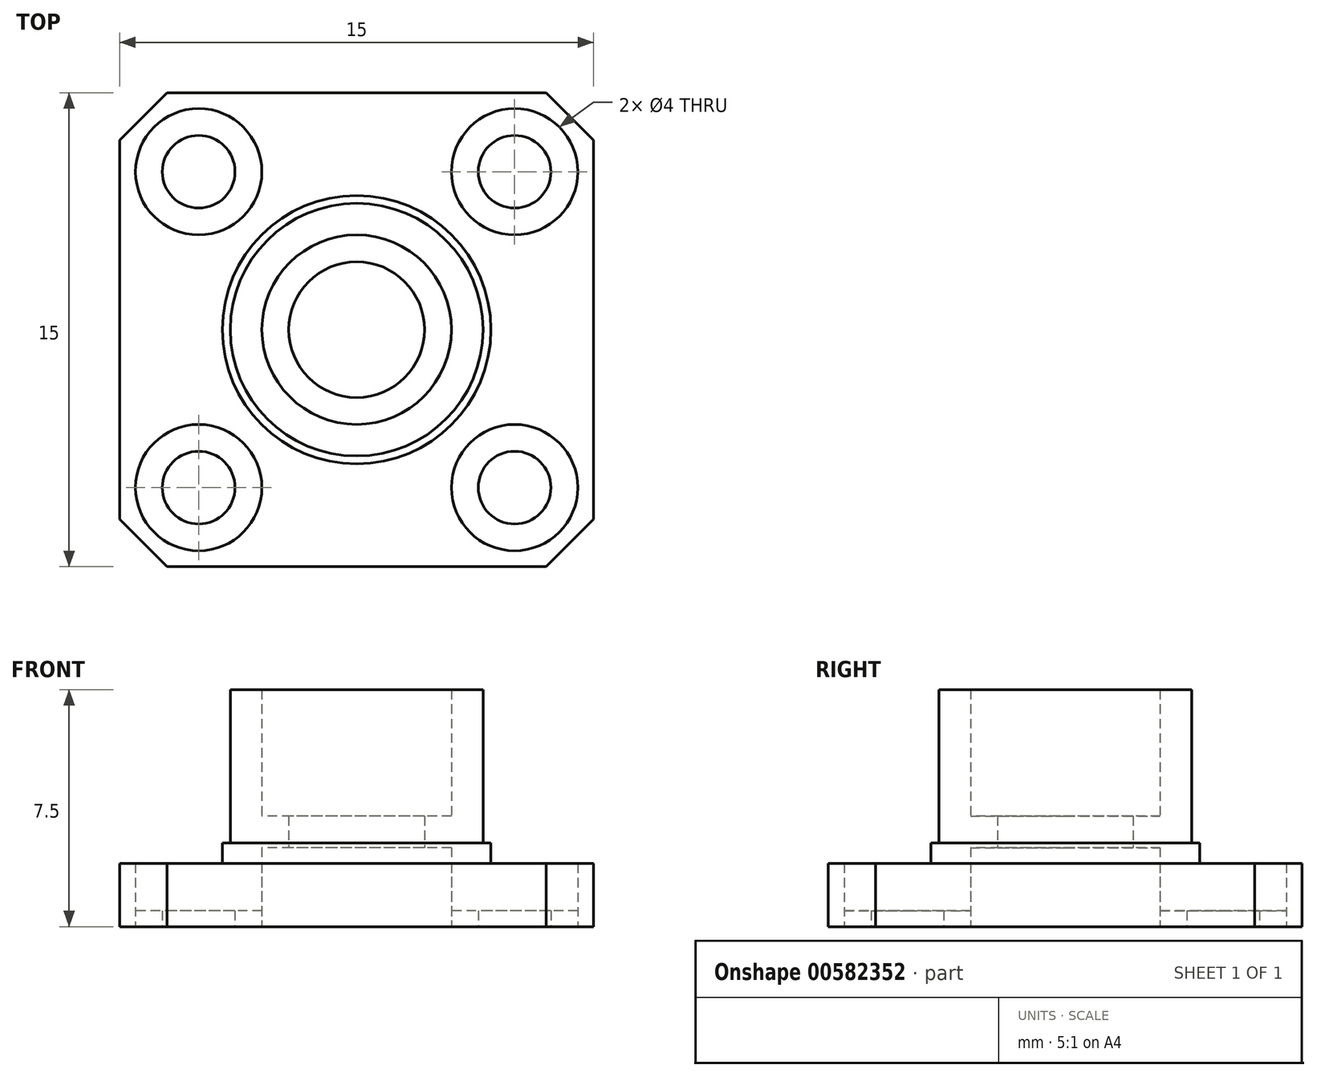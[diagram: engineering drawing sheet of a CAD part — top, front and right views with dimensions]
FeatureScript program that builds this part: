
annotation { "Feature Type Name" : "Feature", "Feature Type Description" : "" }
export const myFeature = defineFeature(function(context is Context, id is Id, definition is map)
    precondition{}
    {
        {
            var Q0;
            Q0=qCreatedBy(makeId("Top.planeOp"),FACE);
            var sketch = newSketch(context, id + "F0", { "sketchPlane" : qUnion([Q0])});
            skLineSegment(sketch, "E0.bottom", {"start": v(7.5, -7.5) * mm, "end": v(-7.5, -7.5) * mm});
            skLineSegment(sketch, "E0.top", {"start": v(7.5, 7.5) * mm, "end": v(-7.5, 7.5) * mm});
            skLineSegment(sketch, "E0.left", {"start": v(7.5, -7.5) * mm, "end": v(7.5, 7.5) * mm});
            skLineSegment(sketch, "E0.right", {"start": v(-7.5, -7.5) * mm, "end": v(-7.5, 7.5) * mm});
            skPoint(sketch, "E0.middle", {"position": v(0, 0) * mm});
            skCircle(sketch, "E1", {"center": v(0, 0) * mm, "radius": 4.25 * mm});
            skCircle(sketch, "E2", {"center": v(0, 0) * mm, "radius": 4 * mm});
            skCircle(sketch, "E3", {"center": v(0, 0) * mm, "radius": 3 * mm});
            skCircle(sketch, "E4", {"center": v(0, 0) * mm, "radius": 2.15 * mm});
            skCircle(sketch, "E5", {"center": v(-5, 5) * mm, "radius": 1.15 * mm});
            skCircle(sketch, "E6.MirrorC", {"center": v(5, 5) * mm, "radius": 1.15 * mm});
            skCircle(sketch, "E7.MirrorC", {"center": v(5, -5) * mm, "radius": 1.15 * mm});
            skCircle(sketch, "E8.MirrorC", {"center": v(-5, -5) * mm, "radius": 1.15 * mm});
            skCircle(sketch, "E9.0", {"center": v(0, 0) * mm, "radius": 3.76 * mm});
            skCircle(sketch, "E10", {"center": v(-5, 5) * mm, "radius": 2 * mm});
            skCircle(sketch, "E11", {"center": v(5, 5) * mm, "radius": 2 * mm});
            skCircle(sketch, "E12", {"center": v(-5, -5) * mm, "radius": 2 * mm});
            skCircle(sketch, "E13", {"center": v(5, -5) * mm, "radius": 2 * mm});
            skSolve(sketch);
        }
        {
            var Q0;
            Q0=makeQuery(id+"F0.imprint","IMPRINT",FACE,{"disambiguationData":[TD([[makeQuery(id+"F0.imprint","IMPRINT",EDGE,{"derivedFrom":sQuery(id+"F0.wireOp",EDGE,"E0.bottom")}),-1.0]])]});
            extrude(context, id + "F1", {"entities" : qUnion([Q0]), "depth" : 2 * mm, "offsetDistance" : 25 * mm});
        }
        {
            var Q0;
            Q0=makeQuery(id+"F0.imprint","IMPRINT",FACE,{"disambiguationData":[TD([[makeQuery(id+"F0.imprint","IMPRINT",EDGE,{"derivedFrom":sQuery(id+"F0.wireOp",EDGE,"E1")}),1.0]])]});
            extrude(context, id + "F2", {"entities" : qUnion([Q0]), "operationType" : NewBodyOperationType.ADD, "depth" : 2.65 * mm, "offsetDistance" : 25 * mm});
        }
        {
            var Q0;
            Q0=makeQuery(id+"F0.imprint","IMPRINT",FACE,{"disambiguationData":[TD([[makeQuery(id+"F0.imprint","IMPRINT",EDGE,{"derivedFrom":sQuery(id+"F0.wireOp",EDGE,"E2")}),1.0]])]});
            var Q1;
            Q1=makeQuery(id+"F0.imprint","IMPRINT",FACE,{"disambiguationData":[TD([[makeQuery(id+"F0.imprint","IMPRINT",EDGE,{"derivedFrom":sQuery(id+"F0.wireOp",EDGE,"E3")}),-1.0]])]});
            extrude(context, id + "F3", {"entities" : qUnion([Q0, Q1]), "operationType" : NewBodyOperationType.ADD, "depth" : 7.5 * mm, "offsetDistance" : 25 * mm});
        }
        {
            var Q0;
            Q0=makeQuery(id+"F0.imprint","IMPRINT",FACE,{"disambiguationData":[TD([[makeQuery(id+"F0.imprint","IMPRINT",EDGE,{"derivedFrom":sQuery(id+"F0.wireOp",EDGE,"E3")}),1.0]])]});
            var Q1;
            Q1=makeQuery(id+"F0.imprint","IMPRINT",FACE,{"disambiguationData":[TD([[makeQuery(id+"F0.imprint","IMPRINT",EDGE,{"derivedFrom":sQuery(id+"F0.wireOp",EDGE,"E3")}),-1.0]])]});
            extrude(context, id + "F4", {"entities" : qUnion([Q0, Q1]), "operationType" : NewBodyOperationType.ADD, "depth" : (7.5 - 4) * mm, "offsetDistance" : 25 * mm});
        }
        {
            var Q0;
            Q0=makeQuery(id+"F0.imprint","IMPRINT",FACE,{"disambiguationData":[TD([[makeQuery(id+"F0.imprint","IMPRINT",EDGE,{"derivedFrom":sQuery(id+"F0.wireOp",EDGE,"E3")}),1.0]])]});
            extrude(context, id + "F5", {"entities" : qUnion([Q0]), "operationType" : NewBodyOperationType.REMOVE, "depth" : 2.5 * mm, "offsetDistance" : 25 * mm});
        }
        {
            var Q0;
            Q0=makeQuery(id+"F1.opExtrude","SWEPT_EDGE",EDGE,{"disambiguationData":[OSD([sQuery(id+"F0.wireOp",EDGE,"E0.bottom"),sQuery(id+"F0.wireOp",EDGE,"E0.left")])]});
            var Q1;
            Q1=makeQuery(id+"F1.opExtrude","SWEPT_EDGE",EDGE,{"disambiguationData":[OSD([sQuery(id+"F0.wireOp",EDGE,"E0.top"),sQuery(id+"F0.wireOp",EDGE,"E0.left")])]});
            var Q2;
            Q2=makeQuery(id+"F1.opExtrude","SWEPT_EDGE",EDGE,{"disambiguationData":[OSD([sQuery(id+"F0.wireOp",EDGE,"E0.bottom"),sQuery(id+"F0.wireOp",EDGE,"E0.right")])]});
            var Q3;
            Q3=makeQuery(id+"F1.opExtrude","SWEPT_EDGE",EDGE,{"disambiguationData":[OSD([sQuery(id+"F0.wireOp",EDGE,"E0.top"),sQuery(id+"F0.wireOp",EDGE,"E0.right")])]});
            chamfer(context, id + "F6", {"entities" : qUnion([Q0, Q1, Q2, Q3]), "width" : 1.5 * mm, "tangentPropagation" : true});
        }
        {
            var Q0;
            Q0=makeQuery(id+"F0.imprint","IMPRINT",FACE,{"disambiguationData":[TD([[makeQuery(id+"F0.imprint","IMPRINT",EDGE,{"derivedFrom":sQuery(id+"F0.wireOp",EDGE,"E5")}),-1.0]])]});
            var Q1;
            Q1=makeQuery(id+"F0.imprint","IMPRINT",FACE,{"disambiguationData":[TD([[makeQuery(id+"F0.imprint","IMPRINT",EDGE,{"derivedFrom":sQuery(id+"F0.wireOp",EDGE,"E6.MirrorC")}),1.0]])]});
            var Q2;
            Q2=makeQuery(id+"F0.imprint","IMPRINT",FACE,{"disambiguationData":[TD([[makeQuery(id+"F0.imprint","IMPRINT",EDGE,{"derivedFrom":sQuery(id+"F0.wireOp",EDGE,"E7.MirrorC")}),-1.0]])]});
            var Q3;
            Q3=makeQuery(id+"F0.imprint","IMPRINT",FACE,{"disambiguationData":[TD([[makeQuery(id+"F0.imprint","IMPRINT",EDGE,{"derivedFrom":sQuery(id+"F0.wireOp",EDGE,"E8.MirrorC")}),1.0]])]});
            extrude(context, id + "F7", {"entities" : qUnion([Q0, Q1, Q2, Q3]), "operationType" : NewBodyOperationType.ADD, "depth" : 0.5 * mm, "offsetDistance" : 25 * mm});
        }
    });
